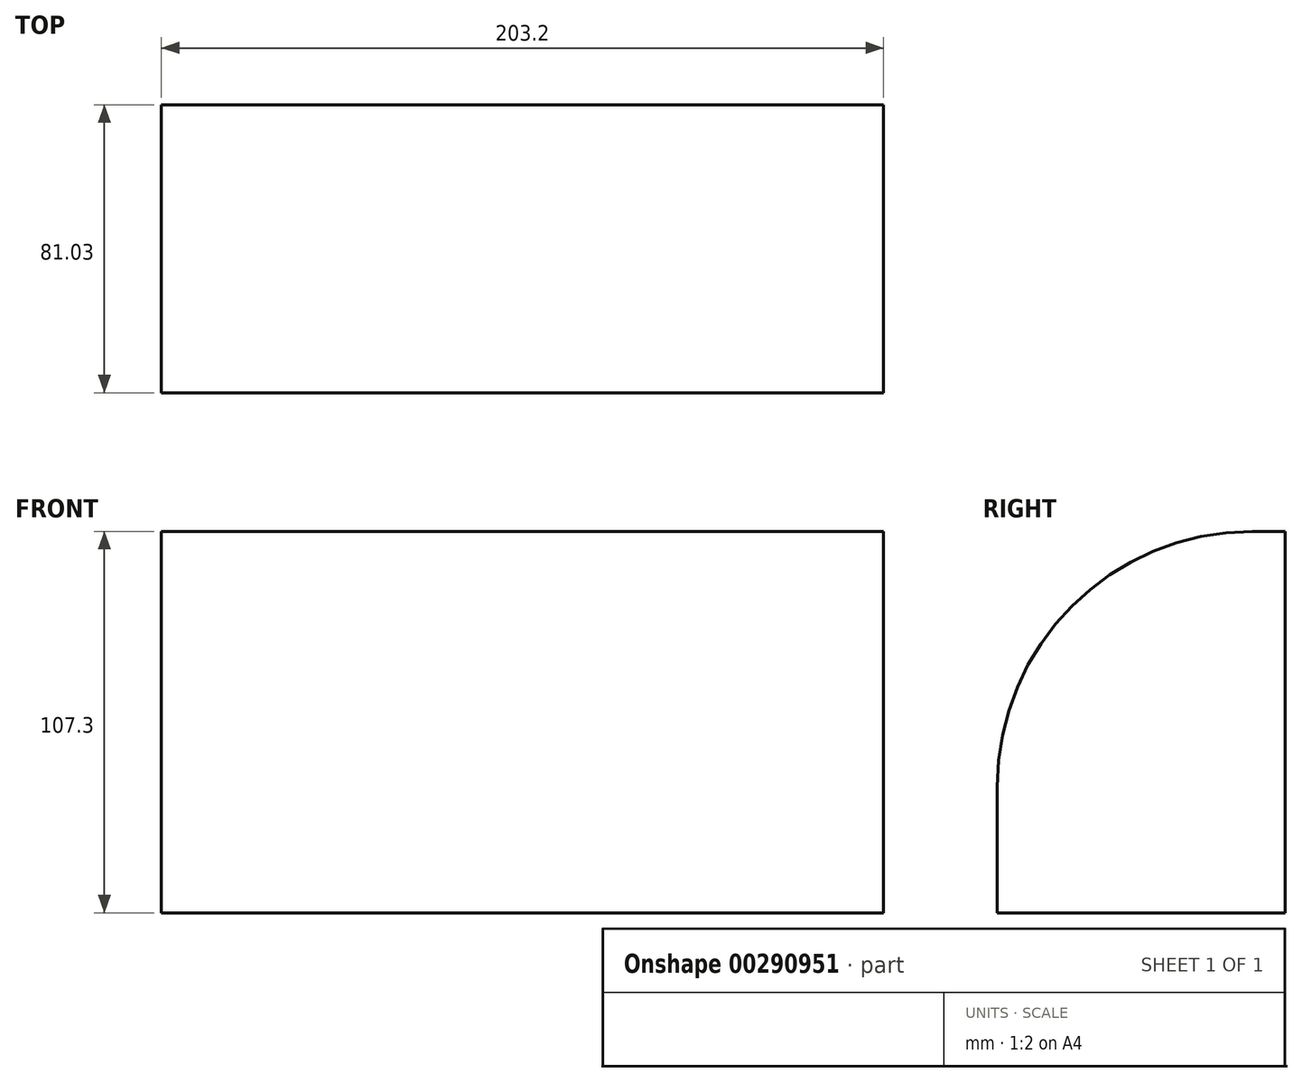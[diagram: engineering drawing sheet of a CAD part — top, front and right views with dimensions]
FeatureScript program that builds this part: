
annotation { "Feature Type Name" : "Feature", "Feature Type Description" : "" }
export const myFeature = defineFeature(function(context is Context, id is Id, definition is map)
    precondition{}
    {
        {
            var Q0;
            Q0=qCreatedBy(makeId("Front.planeOp"),FACE);
            var sketch = newSketch(context, id + "F0", { "sketchPlane" : qUnion([Q0])});
            skLineSegment(sketch, "E0.bottom", {"start": v(-101.6, -53.65) * mm, "end": v(101.6, -53.65) * mm});
            skLineSegment(sketch, "E0.top", {"start": v(-101.6, 53.65) * mm, "end": v(101.6, 53.65) * mm});
            skLineSegment(sketch, "E0.left", {"start": v(-101.6, -53.65) * mm, "end": v(-101.6, 53.65) * mm});
            skLineSegment(sketch, "E0.right", {"start": v(101.6, -53.65) * mm, "end": v(101.6, 53.65) * mm});
            skPoint(sketch, "E0.middle", {"position": v(0, 0) * mm});
            skSolve(sketch);
        }
        {
            var Q0;
            Q0=makeQuery(id+"F0.imprint","IMPRINT",FACE,{"disambiguationData":[TD([[makeQuery(id+"F0.imprint","IMPRINT",EDGE,{"derivedFrom":sQuery(id+"F0.wireOp",EDGE,"E0.bottom")}),1.0]])]});
            extrude(context, id + "F1", {"entities" : qUnion([Q0]), "depth" : 81.03 * mm});
        }
        {
            var Q0;
            Q0=makeQuery(id+"F1.opExtrude","CAP_EDGE",EDGE,{"disambiguationData":[OSD([sQuery(id+"F0.wireOp",EDGE,"E0.top")])],"isStart":false});
            fillet(context, id + "F2", {"entities" : qUnion([Q0]), "radius" : 71.75 * mm, "tangentPropagation" : true, "allowEdgeOverflow" : false});
        }
    });
